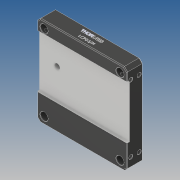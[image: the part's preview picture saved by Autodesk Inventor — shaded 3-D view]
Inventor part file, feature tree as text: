
AUTODESK INVENTOR PART (.ipt)
format: ipt  version: 2019 (Build 230136000, 136)  size: 624,640 bytes
history: native  units: mm
features: sketch x2, extrude x1, hole x1, other x1
ambient origin geometry x8: Origin, YZ Plane, XZ Plane, XY Plane, X Axis, Y Axis, Z Axis, Center Point
bodies: Solid1 (feature_tree)
feature tree (5):
  extrude  "Extrusion1"  Depth=42.0mm
  hole  "Hole1"  [1 undecoded]
  sketch  "Sketch1"  dims[d0=15.55mm d2=42.0mm]
  sketch  "Sketch3"  dims[d3=2.0mm d4=0.0mm d5=14.0mm d6=23.0mm d7=4.25mm d8=19.05mm d9=7.5mm d10=4.5mm d11=14.3117mm d12=25.4mm d13=20.594885mm]
  other  "13108-001-1-solid1"
note: 1 required parameter value undecoded (feature->parameter linkage not recoverable at this tier; creation-order binding heuristic only, values carry confidence <= 0.55)
